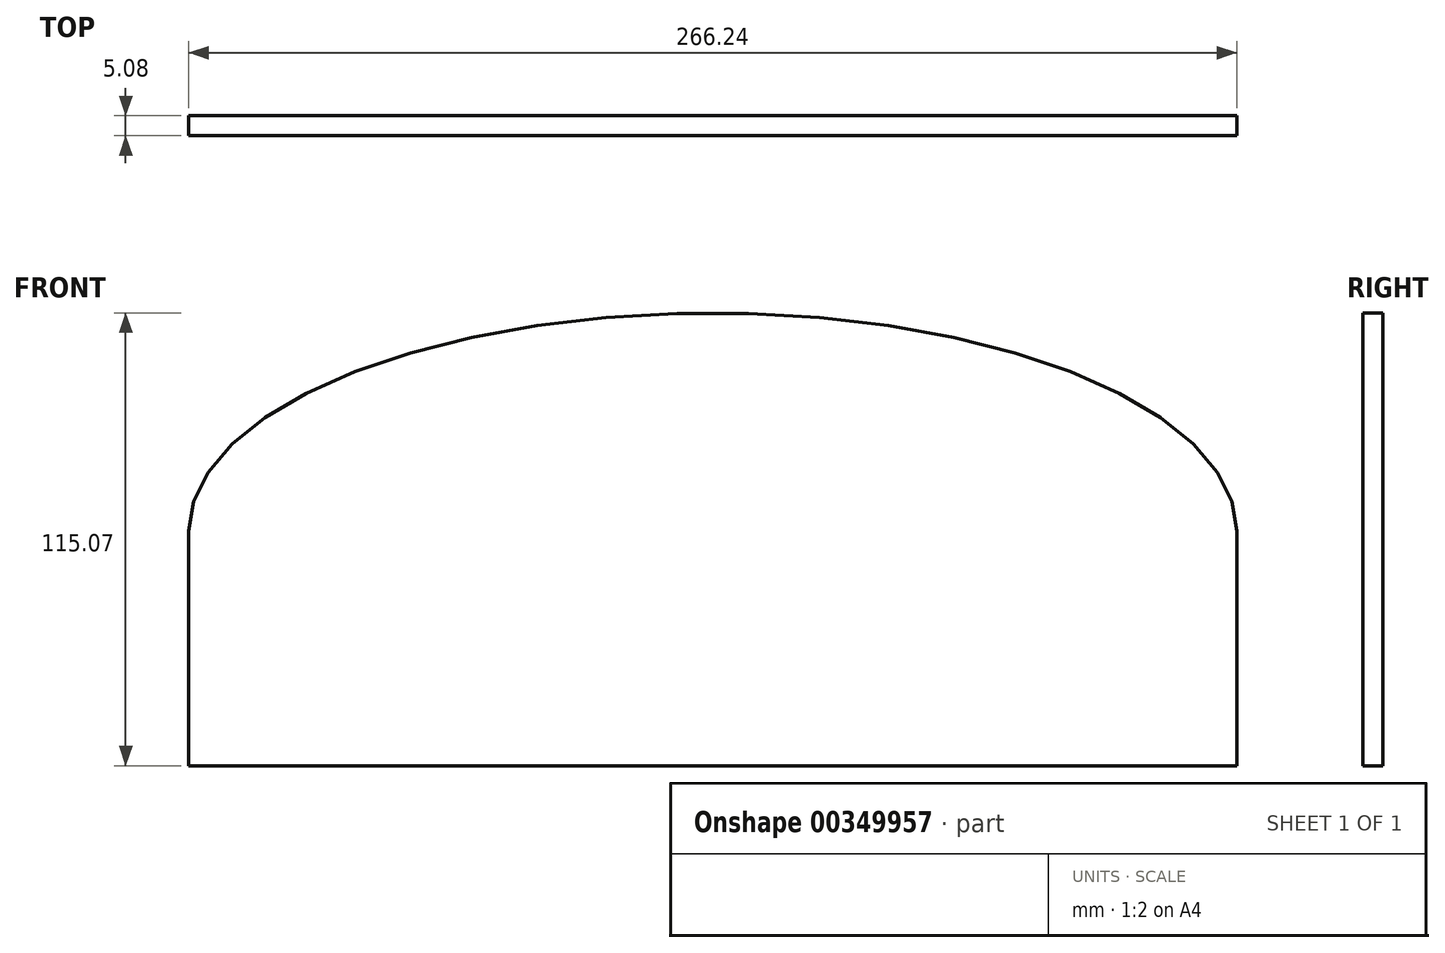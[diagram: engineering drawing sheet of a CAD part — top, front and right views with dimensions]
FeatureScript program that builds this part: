
annotation { "Feature Type Name" : "Feature", "Feature Type Description" : "" }
export const myFeature = defineFeature(function(context is Context, id is Id, definition is map)
    precondition{}
    {
        {
            var Q0;
            Q0=qCreatedBy(makeId("Front.planeOp"),FACE);
            var sketch = newSketch(context, id + "F0", { "sketchPlane" : qUnion([Q0])});
            skEllipse(sketch, "E0", {"center": v(0, 0) * mm, "majorRadius": 133.12 * mm, "minorRadius": 55.46 * mm, "majorAxis": v(1, 0)});
            skLineSegment(sketch, "E1.bottom", {"start": v(-133.12, 0) * mm, "end": v(133.12, 0) * mm});
            skLineSegment(sketch, "E1.top", {"start": v(-133.12, -59.6) * mm, "end": v(133.12, -59.6) * mm});
            skLineSegment(sketch, "E1.left", {"start": v(-133.12, 0) * mm, "end": v(-133.12, -59.6) * mm});
            skLineSegment(sketch, "E1.right", {"start": v(133.12, 0) * mm, "end": v(133.12, -59.6) * mm});
            skSolve(sketch);
        }
        {
            var Q0;
            Q0 = qSketchRegion(id + "F0", true);
            extrude(context, id + "F1", {"entities" : qUnion([Q0]), "depth" : 5.08 * mm});
        }
    });
